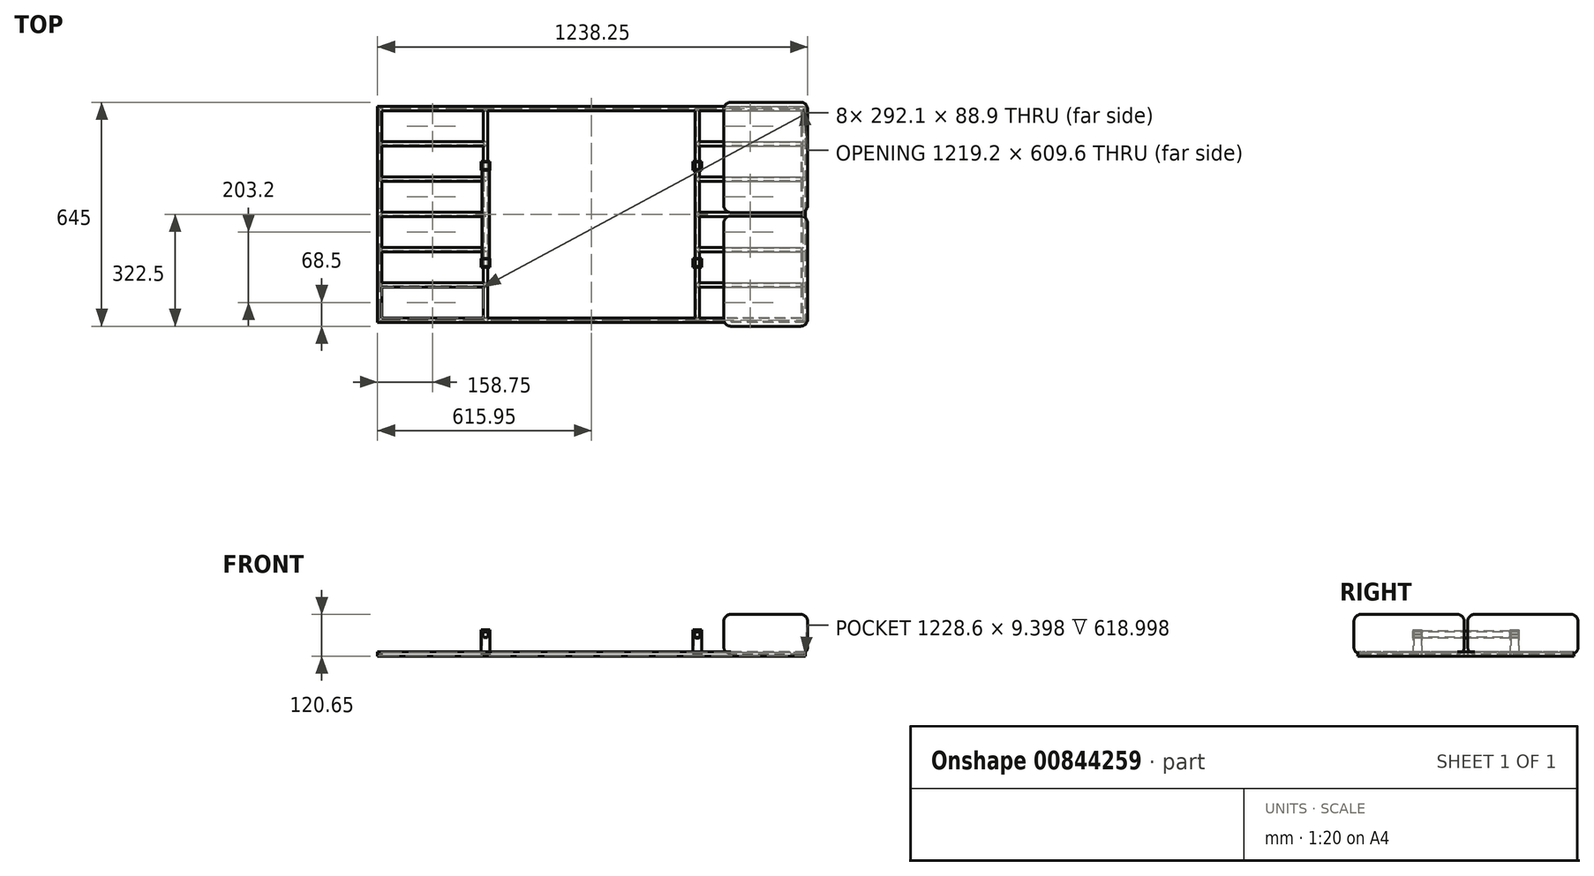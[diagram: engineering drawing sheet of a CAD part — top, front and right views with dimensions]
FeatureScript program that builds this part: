
annotation { "Feature Type Name" : "Feature", "Feature Type Description" : "" }
export const myFeature = defineFeature(function(context is Context, id is Id, definition is map)
    precondition{}
    {
        {
            var Q0;
            Q0=qCreatedBy(makeId("Top.planeOp"),FACE);
            var sketch = newSketch(context, id + "F0", { "sketchPlane" : qUnion([Q0])});
            skLineSegment(sketch, "E0", {"start": v(0, 0) * mm, "end": v(-609.6, 0) * mm});
            skLineSegment(sketch, "E1", {"start": v(-609.6, -609.6) * mm, "end": v(0, -609.6) * mm});
            skLineSegment(sketch, "E2", {"start": v(0, 0) * mm, "end": v(0, -609.6) * mm, "construction": true});
            skLineSegment(sketch, "E3.MirrorCS", {"start": v(609.6, -609.6) * mm, "end": v(0, -609.6) * mm});
            skLineSegment(sketch, "E4.MirrorCS", {"start": v(0, 0) * mm, "end": v(609.6, 0) * mm});
            skLineSegment(sketch, "E5", {"start": v(-304.8, 0) * mm, "end": v(-304.8, -609.6) * mm});
            skLineSegment(sketch, "E6.MirrorCS", {"start": v(304.8, 0) * mm, "end": v(304.8, -609.6) * mm});
            skPoint(sketch, "E7.orphan", {"position": v(508, -304.8) * mm});
            skLineSegment(sketch, "E8", {"start": v(-609.6, 0) * mm, "end": v(-609.6, -609.6) * mm});
            skLineSegment(sketch, "E9", {"start": v(609.6, -609.6) * mm, "end": v(609.6, 0) * mm});
            skLineSegment(sketch, "E10", {"start": v(-609.6, -101.6) * mm, "end": v(-304.8, -101.6) * mm});
            skLineSegment(sketch, "E11", {"start": v(-304.8, -203.2) * mm, "end": v(-609.6, -203.2) * mm});
            skLineSegment(sketch, "E12", {"start": v(-304.8, -304.8) * mm, "end": v(-609.6, -304.8) * mm});
            skLineSegment(sketch, "E13", {"start": v(-304.8, -406.4) * mm, "end": v(-609.6, -406.4) * mm});
            skLineSegment(sketch, "E14", {"start": v(-304.8, -508) * mm, "end": v(-609.6, -508) * mm});
            skLineSegment(sketch, "E15.MirrorCS", {"start": v(304.8, -406.4) * mm, "end": v(609.6, -406.4) * mm});
            skLineSegment(sketch, "E16.MirrorCS", {"start": v(304.8, -203.2) * mm, "end": v(609.6, -203.2) * mm});
            skLineSegment(sketch, "E17.MirrorCS", {"start": v(304.8, -508) * mm, "end": v(609.6, -508) * mm});
            skLineSegment(sketch, "E18.MirrorCS", {"start": v(609.6, -101.6) * mm, "end": v(304.8, -101.6) * mm});
            skLineSegment(sketch, "E19.MirrorCS", {"start": v(304.8, -304.8) * mm, "end": v(609.6, -304.8) * mm});
            skSolve(sketch);
        }
        {
            var Q0;
            Q0=qCreatedBy(makeId("Right.planeOp"),FACE);
            var sketch = newSketch(context, id + "F1", { "sketchPlane" : qUnion([Q0])});
            skLineSegment(sketch, "E20.bottom", {"start": v(-6.35, 6.35) * mm, "end": v(6.35, 6.35) * mm});
            skLineSegment(sketch, "E20.top", {"start": v(-6.35, -6.35) * mm, "end": v(6.35, -6.35) * mm});
            skLineSegment(sketch, "E20.left", {"start": v(-6.35, 6.35) * mm, "end": v(-6.35, -6.35) * mm});
            skLineSegment(sketch, "E20.right", {"start": v(6.35, 6.35) * mm, "end": v(6.35, -6.35) * mm});
            skPoint(sketch, "E20.middle", {"position": v(0, 0) * mm});
            skLineSegment(sketch, "E21.bottom", {"start": v(-4.7, -4.7) * mm, "end": v(4.7, -4.7) * mm});
            skLineSegment(sketch, "E21.top", {"start": v(-4.7, 4.7) * mm, "end": v(4.7, 4.7) * mm});
            skLineSegment(sketch, "E21.left", {"start": v(-4.7, -4.7) * mm, "end": v(-4.7, 4.7) * mm});
            skLineSegment(sketch, "E21.right", {"start": v(4.7, -4.7) * mm, "end": v(4.7, 4.7) * mm});
            skSolve(sketch);
        }
        {
            var Q0;
            Q0=makeQuery(id+"F1.imprint","IMPRINT",FACE,{"disambiguationData":[TD([[makeQuery(id+"F1.imprint","IMPRINT",EDGE,{"derivedFrom":sQuery(id+"F1.wireOp",EDGE,"E20.bottom")}),-1.0]])]});
            var Q1;
            Q1=sQuery(id+"F0.wireOp",EDGE,"E0");
            var Q2;
            Q2=sQuery(id+"F0.wireOp",EDGE,"E8");
            var Q3;
            Q3=sQuery(id+"F0.wireOp",EDGE,"E1");
            var Q4;
            Q4=sQuery(id+"F0.wireOp",EDGE,"E3.MirrorCS");
            var Q5;
            Q5=sQuery(id+"F0.wireOp",EDGE,"E9");
            var Q6;
            Q6=sQuery(id+"F0.wireOp",EDGE,"E4.MirrorCS");
            sweep(context, id + "F2", {"profiles" : qUnion([Q0]), "path" : qUnion([Q1, Q2, Q3, Q4, Q5, Q6])});
        }
        {
            var Q0;
            Q0=qCreatedBy(makeId("Right.planeOp"),FACE);
            cPlane(context, id + "F3", {"entities" : qUnion([Q0]), "cplaneType" : CPlaneType.OFFSET, "offset" : 304.8 * mm, "width" : 150 * mm, "height" : 150 * mm});
        }
        {
            var Q0;
            Q0=qCreatedBy(id+"F3.planeOp",FACE);
            var sketch = newSketch(context, id + "F4", { "sketchPlane" : qUnion([Q0])});
            skCircle(sketch, "E22", {"center": v(-101.6, 0) * mm, "radius": 13.34 * mm, "construction": true});
            skCircle(sketch, "E23", {"center": v(-203.2, 0) * mm, "radius": 13.34 * mm, "construction": true});
            skCircle(sketch, "E24", {"center": v(-304.8, 0) * mm, "radius": 13.34 * mm, "construction": true});
            skCircle(sketch, "E25", {"center": v(-406.4, 0) * mm, "radius": 13.34 * mm, "construction": true});
            skCircle(sketch, "E26", {"center": v(-508, 0) * mm, "radius": 13.34 * mm, "construction": true});
            skCircle(sketch, "E27", {"center": v(-101.6, 0) * mm, "radius": 10.46 * mm, "construction": true});
            skCircle(sketch, "E28", {"center": v(-203.2, 0) * mm, "radius": 10.46 * mm, "construction": true});
            skCircle(sketch, "E29", {"center": v(-304.8, 0) * mm, "radius": 10.46 * mm, "construction": true});
            skCircle(sketch, "E30", {"center": v(-406.4, 0) * mm, "radius": 10.46 * mm, "construction": true});
            skCircle(sketch, "E31", {"center": v(-508, 0) * mm, "radius": 10.46 * mm, "construction": true});
            skLineSegment(sketch, "E32.bottom", {"start": v(-95.25, 6.35) * mm, "end": v(-107.95, 6.35) * mm});
            skLineSegment(sketch, "E32.top", {"start": v(-95.25, -6.35) * mm, "end": v(-107.95, -6.35) * mm});
            skLineSegment(sketch, "E32.left", {"start": v(-95.25, 6.35) * mm, "end": v(-95.25, -6.35) * mm});
            skLineSegment(sketch, "E32.right", {"start": v(-107.95, 6.35) * mm, "end": v(-107.95, -6.35) * mm});
            skLineSegment(sketch, "E33.bottom", {"start": v(-96.9, 4.7) * mm, "end": v(-106.3, 4.7) * mm});
            skLineSegment(sketch, "E33.top", {"start": v(-96.9, -4.7) * mm, "end": v(-106.3, -4.7) * mm});
            skLineSegment(sketch, "E33.left", {"start": v(-96.9, 4.7) * mm, "end": v(-96.9, -4.7) * mm});
            skLineSegment(sketch, "E33.right", {"start": v(-106.3, 4.7) * mm, "end": v(-106.3, -4.7) * mm});
            skLineSegment(sketch, "E34.bottom", {"start": v(-196.85, 6.35) * mm, "end": v(-209.55, 6.35) * mm});
            skLineSegment(sketch, "E34.top", {"start": v(-196.85, -6.35) * mm, "end": v(-209.55, -6.35) * mm});
            skLineSegment(sketch, "E34.left", {"start": v(-196.85, 6.35) * mm, "end": v(-196.85, -6.35) * mm});
            skLineSegment(sketch, "E34.right", {"start": v(-209.55, 6.35) * mm, "end": v(-209.55, -6.35) * mm});
            skLineSegment(sketch, "E35.bottom", {"start": v(-298.45, 6.35) * mm, "end": v(-311.15, 6.35) * mm});
            skLineSegment(sketch, "E35.top", {"start": v(-298.45, -6.35) * mm, "end": v(-311.15, -6.35) * mm});
            skLineSegment(sketch, "E35.left", {"start": v(-298.45, 6.35) * mm, "end": v(-298.45, -6.35) * mm});
            skLineSegment(sketch, "E35.right", {"start": v(-311.15, 6.35) * mm, "end": v(-311.15, -6.35) * mm});
            skLineSegment(sketch, "E36.bottom", {"start": v(-400.05, 6.35) * mm, "end": v(-412.75, 6.35) * mm});
            skLineSegment(sketch, "E36.top", {"start": v(-400.05, -6.35) * mm, "end": v(-412.75, -6.35) * mm});
            skLineSegment(sketch, "E36.left", {"start": v(-400.05, 6.35) * mm, "end": v(-400.05, -6.35) * mm});
            skLineSegment(sketch, "E36.right", {"start": v(-412.75, 6.35) * mm, "end": v(-412.75, -6.35) * mm});
            skLineSegment(sketch, "E37.bottom", {"start": v(-501.65, 6.35) * mm, "end": v(-514.35, 6.35) * mm});
            skLineSegment(sketch, "E37.top", {"start": v(-501.65, -6.35) * mm, "end": v(-514.35, -6.35) * mm});
            skLineSegment(sketch, "E37.left", {"start": v(-501.65, 6.35) * mm, "end": v(-501.65, -6.35) * mm});
            skLineSegment(sketch, "E37.right", {"start": v(-514.35, 6.35) * mm, "end": v(-514.35, -6.35) * mm});
            skLineSegment(sketch, "E38.bottom", {"start": v(-503.3, 4.7) * mm, "end": v(-512.7, 4.7) * mm});
            skLineSegment(sketch, "E38.top", {"start": v(-503.3, -4.7) * mm, "end": v(-512.7, -4.7) * mm});
            skLineSegment(sketch, "E38.left", {"start": v(-503.3, 4.7) * mm, "end": v(-503.3, -4.7) * mm});
            skLineSegment(sketch, "E38.right", {"start": v(-512.7, 4.7) * mm, "end": v(-512.7, -4.7) * mm});
            skLineSegment(sketch, "E39.bottom", {"start": v(-401.7, 4.7) * mm, "end": v(-411.1, 4.7) * mm});
            skLineSegment(sketch, "E39.top", {"start": v(-401.7, -4.7) * mm, "end": v(-411.1, -4.7) * mm});
            skLineSegment(sketch, "E39.left", {"start": v(-401.7, 4.7) * mm, "end": v(-401.7, -4.7) * mm});
            skLineSegment(sketch, "E39.right", {"start": v(-411.1, 4.7) * mm, "end": v(-411.1, -4.7) * mm});
            skLineSegment(sketch, "E40.bottom", {"start": v(-300.1, 4.7) * mm, "end": v(-309.5, 4.7) * mm});
            skLineSegment(sketch, "E40.top", {"start": v(-300.1, -4.7) * mm, "end": v(-309.5, -4.7) * mm});
            skLineSegment(sketch, "E40.left", {"start": v(-300.1, 4.7) * mm, "end": v(-300.1, -4.7) * mm});
            skLineSegment(sketch, "E40.right", {"start": v(-309.5, 4.7) * mm, "end": v(-309.5, -4.7) * mm});
            skLineSegment(sketch, "E41.bottom", {"start": v(-198.5, 4.7) * mm, "end": v(-207.9, 4.7) * mm});
            skLineSegment(sketch, "E41.top", {"start": v(-198.5, -4.7) * mm, "end": v(-207.9, -4.7) * mm});
            skLineSegment(sketch, "E41.left", {"start": v(-198.5, 4.7) * mm, "end": v(-198.5, -4.7) * mm});
            skLineSegment(sketch, "E41.right", {"start": v(-207.9, 4.7) * mm, "end": v(-207.9, -4.7) * mm});
            skSolve(sketch);
        }
        {
            var Q0;
            Q0 = qSketchRegion(id + "F4", true);
            var Q1;
            Q1=sQuery(id+"F0.wireOp",EDGE,"E17.MirrorCS");
            sweep(context, id + "F5", {"operationType" : NewBodyOperationType.ADD, "profiles" : qUnion([Q0]), "path" : qUnion([Q1])});
        }
        {
            var Q0;
            Q0=qCreatedBy(makeId("Right.planeOp"),FACE);
            cPlane(context, id + "F6", {"entities" : qUnion([Q0]), "cplaneType" : CPlaneType.OFFSET, "offset" : 304.8 * mm, "oppositeDirection" : true, "width" : 150 * mm, "height" : 150 * mm});
        }
        {
            var Q0;
            Q0=qCreatedBy(id+"F6.planeOp",FACE);
            var sketch = newSketch(context, id + "F7", { "sketchPlane" : qUnion([Q0])});
            skCircle(sketch, "E42", {"center": v(-101.6, 0) * mm, "radius": 13.33 * mm, "construction": true});
            skCircle(sketch, "E43", {"center": v(-203.2, 0) * mm, "radius": 13.34 * mm, "construction": true});
            skCircle(sketch, "E44", {"center": v(-304.8, 0) * mm, "radius": 13.34 * mm, "construction": true});
            skCircle(sketch, "E45", {"center": v(-406.4, 0) * mm, "radius": 13.34 * mm, "construction": true});
            skCircle(sketch, "E46", {"center": v(-508, 0) * mm, "radius": 13.34 * mm, "construction": true});
            skCircle(sketch, "E47.0", {"center": v(-101.6, 0) * mm, "radius": 10.46 * mm, "construction": true});
            skCircle(sketch, "E48.0", {"center": v(-203.2, 0) * mm, "radius": 10.46 * mm, "construction": true});
            skCircle(sketch, "E49.0", {"center": v(-304.8, 0) * mm, "radius": 10.46 * mm, "construction": true});
            skCircle(sketch, "E50.0", {"center": v(-406.4, 0) * mm, "radius": 10.46 * mm, "construction": true});
            skCircle(sketch, "E51.0", {"center": v(-508, 0) * mm, "radius": 10.46 * mm, "construction": true});
            skLineSegment(sketch, "E52.bottom", {"start": v(-95.25, 6.35) * mm, "end": v(-107.95, 6.35) * mm});
            skLineSegment(sketch, "E52.top", {"start": v(-95.25, -6.35) * mm, "end": v(-107.95, -6.35) * mm});
            skLineSegment(sketch, "E52.left", {"start": v(-95.25, 6.35) * mm, "end": v(-95.25, -6.35) * mm});
            skLineSegment(sketch, "E52.right", {"start": v(-107.95, 6.35) * mm, "end": v(-107.95, -6.35) * mm});
            skLineSegment(sketch, "E53.bottom", {"start": v(-96.9, 4.7) * mm, "end": v(-106.3, 4.7) * mm});
            skLineSegment(sketch, "E53.top", {"start": v(-96.9, -4.7) * mm, "end": v(-106.3, -4.7) * mm});
            skLineSegment(sketch, "E53.left", {"start": v(-96.9, 4.7) * mm, "end": v(-96.9, -4.7) * mm});
            skLineSegment(sketch, "E53.right", {"start": v(-106.3, 4.7) * mm, "end": v(-106.3, -4.7) * mm});
            skLineSegment(sketch, "E54.1.0.0", {"start": v(-196.85, 6.35) * mm, "end": v(-209.55, 6.35) * mm});
            skLineSegment(sketch, "E54.1.0.1", {"start": v(-209.55, 6.35) * mm, "end": v(-209.55, -6.35) * mm});
            skLineSegment(sketch, "E54.1.0.2", {"start": v(-196.85, -6.35) * mm, "end": v(-209.55, -6.35) * mm});
            skLineSegment(sketch, "E54.1.0.3", {"start": v(-196.85, 6.35) * mm, "end": v(-196.85, -6.35) * mm});
            skLineSegment(sketch, "E54.1.0.4", {"start": v(-198.5, 4.7) * mm, "end": v(-198.5, -4.7) * mm});
            skLineSegment(sketch, "E54.1.0.5", {"start": v(-198.5, 4.7) * mm, "end": v(-207.9, 4.7) * mm});
            skLineSegment(sketch, "E54.1.0.6", {"start": v(-207.9, 4.7) * mm, "end": v(-207.9, -4.7) * mm});
            skLineSegment(sketch, "E54.1.0.7", {"start": v(-198.5, -4.7) * mm, "end": v(-207.9, -4.7) * mm});
            skLineSegment(sketch, "E54.2.0.0", {"start": v(-298.45, 6.35) * mm, "end": v(-311.15, 6.35) * mm});
            skLineSegment(sketch, "E54.2.0.1", {"start": v(-311.15, 6.35) * mm, "end": v(-311.15, -6.35) * mm});
            skLineSegment(sketch, "E54.2.0.2", {"start": v(-298.45, -6.35) * mm, "end": v(-311.15, -6.35) * mm});
            skLineSegment(sketch, "E54.2.0.3", {"start": v(-298.45, 6.35) * mm, "end": v(-298.45, -6.35) * mm});
            skLineSegment(sketch, "E54.2.0.4", {"start": v(-300.1, 4.7) * mm, "end": v(-300.1, -4.7) * mm});
            skLineSegment(sketch, "E54.2.0.5", {"start": v(-300.1, 4.7) * mm, "end": v(-309.5, 4.7) * mm});
            skLineSegment(sketch, "E54.2.0.6", {"start": v(-309.5, 4.7) * mm, "end": v(-309.5, -4.7) * mm});
            skLineSegment(sketch, "E54.2.0.7", {"start": v(-300.1, -4.7) * mm, "end": v(-309.5, -4.7) * mm});
            skLineSegment(sketch, "E54.3.0.0", {"start": v(-400.05, 6.35) * mm, "end": v(-412.75, 6.35) * mm});
            skLineSegment(sketch, "E54.3.0.1", {"start": v(-412.75, 6.35) * mm, "end": v(-412.75, -6.35) * mm});
            skLineSegment(sketch, "E54.3.0.2", {"start": v(-400.05, -6.35) * mm, "end": v(-412.75, -6.35) * mm});
            skLineSegment(sketch, "E54.3.0.3", {"start": v(-400.05, 6.35) * mm, "end": v(-400.05, -6.35) * mm});
            skLineSegment(sketch, "E54.3.0.4", {"start": v(-401.7, 4.7) * mm, "end": v(-401.7, -4.7) * mm});
            skLineSegment(sketch, "E54.3.0.5", {"start": v(-401.7, 4.7) * mm, "end": v(-411.1, 4.7) * mm});
            skLineSegment(sketch, "E54.3.0.6", {"start": v(-411.1, 4.7) * mm, "end": v(-411.1, -4.7) * mm});
            skLineSegment(sketch, "E54.3.0.7", {"start": v(-401.7, -4.7) * mm, "end": v(-411.1, -4.7) * mm});
            skLineSegment(sketch, "E54.4.0.0", {"start": v(-501.65, 6.35) * mm, "end": v(-514.35, 6.35) * mm});
            skLineSegment(sketch, "E54.4.0.1", {"start": v(-514.35, 6.35) * mm, "end": v(-514.35, -6.35) * mm});
            skLineSegment(sketch, "E54.4.0.2", {"start": v(-501.65, -6.35) * mm, "end": v(-514.35, -6.35) * mm});
            skLineSegment(sketch, "E54.4.0.3", {"start": v(-501.65, 6.35) * mm, "end": v(-501.65, -6.35) * mm});
            skLineSegment(sketch, "E54.4.0.4", {"start": v(-503.3, 4.7) * mm, "end": v(-503.3, -4.7) * mm});
            skLineSegment(sketch, "E54.4.0.5", {"start": v(-503.3, 4.7) * mm, "end": v(-512.7, 4.7) * mm});
            skLineSegment(sketch, "E54.4.0.6", {"start": v(-512.7, 4.7) * mm, "end": v(-512.7, -4.7) * mm});
            skLineSegment(sketch, "E54.4.0.7", {"start": v(-503.3, -4.7) * mm, "end": v(-512.7, -4.7) * mm});
            skLineSegment(sketch, "E54.direction1", {"start": v(-107.95, 6.35) * mm, "end": v(-209.55, 6.35) * mm, "construction": true});
            skSolve(sketch);
        }
        {
            var Q0;
            Q0 = qSketchRegion(id + "F7", true);
            var Q1;
            Q1=sQuery(id+"F0.wireOp",EDGE,"E14");
            sweep(context, id + "F8", {"operationType" : NewBodyOperationType.ADD, "profiles" : qUnion([Q0]), "path" : qUnion([Q1])});
        }
        {
            var Q0;
            Q0=qCreatedBy(makeId("Front.planeOp"),FACE);
            cPlane(context, id + "F9", {"entities" : qUnion([Q0]), "cplaneType" : CPlaneType.OFFSET, "offset" : (609.6 / 2) * mm, "width" : 150 * mm, "height" : 150 * mm});
        }
        {
            var Q0;
            Q0=qCreatedBy(id+"F9.planeOp",FACE);
            var sketch = newSketch(context, id + "F10", { "sketchPlane" : qUnion([Q0])});
            skCircle(sketch, "E55", {"center": v(-304.8, 0) * mm, "radius": 13.34 * mm, "construction": true});
            skLineSegment(sketch, "E56", {"start": v(0, 161.47) * mm, "end": v(0, -177.5) * mm, "construction": true});
            skCircle(sketch, "E57.MirrorC", {"center": v(304.8, 0) * mm, "radius": 13.34 * mm, "construction": true});
            skCircle(sketch, "E58", {"center": v(-304.8, 0) * mm, "radius": 10.46 * mm, "construction": true});
            skCircle(sketch, "E59", {"center": v(304.8, 0) * mm, "radius": 10.46 * mm, "construction": true});
            skLineSegment(sketch, "E60.bottom", {"start": v(-298.45, 6.35) * mm, "end": v(-311.15, 6.35) * mm});
            skLineSegment(sketch, "E60.top", {"start": v(-298.45, -6.35) * mm, "end": v(-311.15, -6.35) * mm});
            skLineSegment(sketch, "E60.left", {"start": v(-298.45, 6.35) * mm, "end": v(-298.45, -6.35) * mm});
            skLineSegment(sketch, "E60.right", {"start": v(-311.15, 6.35) * mm, "end": v(-311.15, -6.35) * mm});
            skLineSegment(sketch, "E61.bottom", {"start": v(-300.1, 4.7) * mm, "end": v(-309.5, 4.7) * mm});
            skLineSegment(sketch, "E61.top", {"start": v(-300.1, -4.7) * mm, "end": v(-309.5, -4.7) * mm});
            skLineSegment(sketch, "E61.left", {"start": v(-300.1, 4.7) * mm, "end": v(-300.1, -4.7) * mm});
            skLineSegment(sketch, "E61.right", {"start": v(-309.5, 4.7) * mm, "end": v(-309.5, -4.7) * mm});
            skLineSegment(sketch, "E62.MirrorCS", {"start": v(298.45, 6.35) * mm, "end": v(311.15, 6.35) * mm});
            skLineSegment(sketch, "E63.MirrorCS", {"start": v(300.1, 4.7) * mm, "end": v(309.5, 4.7) * mm});
            skLineSegment(sketch, "E64.MirrorCS", {"start": v(298.45, 6.35) * mm, "end": v(298.45, -6.35) * mm});
            skLineSegment(sketch, "E65.MirrorCS", {"start": v(300.1, 4.7) * mm, "end": v(300.1, -4.7) * mm});
            skLineSegment(sketch, "E66.MirrorCS", {"start": v(300.1, -4.7) * mm, "end": v(309.5, -4.7) * mm});
            skLineSegment(sketch, "E67.MirrorCS", {"start": v(298.45, -6.35) * mm, "end": v(311.15, -6.35) * mm});
            skLineSegment(sketch, "E68.MirrorCS", {"start": v(309.5, 4.7) * mm, "end": v(309.5, -4.7) * mm});
            skLineSegment(sketch, "E69.MirrorCS", {"start": v(311.15, 6.35) * mm, "end": v(311.15, -6.35) * mm});
            skSolve(sketch);
        }
        {
            var Q0;
            Q0=makeQuery(id+"F10.imprint","IMPRINT",FACE,{"disambiguationData":[TD([[makeQuery(id+"F10.imprint","IMPRINT",EDGE,{"derivedFrom":sQuery(id+"F10.wireOp",EDGE,"E60.bottom")}),1.0]])]});
            var Q1;
            Q1=makeQuery(id+"F10.imprint","IMPRINT",FACE,{"disambiguationData":[TD([[makeQuery(id+"F10.imprint","IMPRINT",EDGE,{"derivedFrom":sQuery(id+"F10.wireOp",EDGE,"E62.MirrorCS")}),-1.0]])]});
            var Q2;
            Q2=sQuery(id+"F0.wireOp",EDGE,"E5");
            sweep(context, id + "F11", {"operationType" : NewBodyOperationType.ADD, "profiles" : qUnion([Q0, Q1]), "path" : qUnion([Q2])});
        }
        {
            var Q0;
            Q0=qCreatedBy(makeId("Top.planeOp"),FACE);
            var sketch = newSketch(context, id + "F12", { "sketchPlane" : qUnion([Q0])});
            skLineSegment(sketch, "E70.bottom", {"start": v(622.3, 17.7) * mm, "end": v(381, 17.7) * mm});
            skLineSegment(sketch, "E70.top", {"start": v(622.3, -299.8) * mm, "end": v(381, -299.8) * mm});
            skLineSegment(sketch, "E70.left", {"start": v(622.3, 17.7) * mm, "end": v(622.3, -299.8) * mm});
            skLineSegment(sketch, "E70.right", {"start": v(381, 17.7) * mm, "end": v(381, -299.8) * mm});
            skPoint(sketch, "E70.middle", {"position": v(501.65, -141.05) * mm});
            skPoint(sketch, "E71.0", {"position": v(508, -304.8) * mm});
            skLineSegment(sketch, "E72.0", {"start": v(304.8, 0) * mm, "end": v(304.8, -609.6) * mm, "construction": true});
            skLineSegment(sketch, "E73", {"start": v(508, -304.8) * mm, "end": v(752.08, -304.8) * mm, "construction": true});
            skLineSegment(sketch, "E74.MirrorCS", {"start": v(622.3, -309.8) * mm, "end": v(381, -309.8) * mm});
            skLineSegment(sketch, "E75.MirrorCS", {"start": v(622.3, -627.3) * mm, "end": v(622.3, -309.8) * mm});
            skLineSegment(sketch, "E76.MirrorCS", {"start": v(622.3, -627.3) * mm, "end": v(381, -627.3) * mm});
            skLineSegment(sketch, "E77.MirrorCS", {"start": v(381, -627.3) * mm, "end": v(381, -309.8) * mm});
            skSolve(sketch);
        }
        {
            var Q0;
            Q0 = qSketchRegion(id + "F12", true);
            extrude(context, id + "F13", {"entities" : qUnion([Q0]), "depth" : 114.3 * mm, "offsetDistance" : 25 * mm});
        }
        {
            var Q0;
            Q0=makeQuery(id+"F13.opExtrude","CAP_FACE",FACE,{"disambiguationData":[OSD([sQuery(id+"F12.wireOp",EDGE,"E70.bottom"),sQuery(id+"F12.wireOp",EDGE,"E70.top"),sQuery(id+"F12.wireOp",EDGE,"E70.left"),sQuery(id+"F12.wireOp",EDGE,"E70.right")])],"isStart":false});
            var Q1;
            Q1=makeQuery(id+"F13.opExtrude","CAP_FACE",FACE,{"disambiguationData":[OSD([sQuery(id+"F12.wireOp",EDGE,"E74.MirrorCS"),sQuery(id+"F12.wireOp",EDGE,"E75.MirrorCS"),sQuery(id+"F12.wireOp",EDGE,"E76.MirrorCS"),sQuery(id+"F12.wireOp",EDGE,"E77.MirrorCS")])],"isStart":false});
            var Q2;
            Q2=makeQuery(id+"F13.opExtrude","SWEPT_FACE",FACE,{"disambiguationData":[OSD([sQuery(id+"F12.wireOp",EDGE,"E75.MirrorCS")])]});
            var Q3;
            Q3=makeQuery(id+"F13.opExtrude","SWEPT_FACE",FACE,{"disambiguationData":[OSD([sQuery(id+"F12.wireOp",EDGE,"E70.left")])]});
            var Q4;
            Q4=makeQuery(id+"F13.opExtrude","CAP_FACE",FACE,{"disambiguationData":[OSD([sQuery(id+"F12.wireOp",EDGE,"E70.bottom"),sQuery(id+"F12.wireOp",EDGE,"E70.top"),sQuery(id+"F12.wireOp",EDGE,"E70.left"),sQuery(id+"F12.wireOp",EDGE,"E70.right")])],"isStart":true});
            var Q5;
            Q5=makeQuery(id+"F13.opExtrude","CAP_FACE",FACE,{"disambiguationData":[OSD([sQuery(id+"F12.wireOp",EDGE,"E74.MirrorCS"),sQuery(id+"F12.wireOp",EDGE,"E75.MirrorCS"),sQuery(id+"F12.wireOp",EDGE,"E76.MirrorCS"),sQuery(id+"F12.wireOp",EDGE,"E77.MirrorCS")])],"isStart":true});
            var Q6;
            Q6=makeQuery(id+"F13.opExtrude","SWEPT_FACE",FACE,{"disambiguationData":[OSD([sQuery(id+"F12.wireOp",EDGE,"E77.MirrorCS")])]});
            var Q7;
            Q7=makeQuery(id+"F13.opExtrude","SWEPT_FACE",FACE,{"disambiguationData":[OSD([sQuery(id+"F12.wireOp",EDGE,"E70.right")])]});
            fillet(context, id + "F14", {"entities" : qUnion([Q0, Q1, Q2, Q3, Q4, Q5, Q6, Q7]), "radius" : 20 * mm, "tangentPropagation" : true, "allowEdgeOverflow" : false});
        }
        {
            var Q0;
            {var subQ0=sQuery(id+"F0.wireOp",EDGE,"E5");var subQ1=sQuery(id+"F0.wireOp",EDGE,"E14");var subQ2=sQuery(id+"F0.wireOp",EDGE,"E17.MirrorCS");Q0=makeQuery(id+"F11.boolean.opBoolean","MERGE",FACE,{"derivedFrom":[makeQuery(id+"F8.boolean.opBoolean","MERGE",FACE,{"derivedFrom":[makeQuery(id+"F5.boolean.opBoolean","MERGE",FACE,{"derivedFrom":[makeQuery(id+"F2.opSweep","SWEPT_FACE",FACE,{"disambiguationData":[OSD([sQuery(id+"F0.wireOp",EDGE,"E8"),sQuery(id+"F1.wireOp",EDGE,"E20.top")])]}),makeQuery(id+"F5.opSweep","SWEPT_FACE",FACE,{"disambiguationData":[OSD([subQ2,sQuery(id+"F4.wireOp",EDGE,"E32.top")])]}),makeQuery(id+"F5.opSweep","SWEPT_FACE",FACE,{"disambiguationData":[OSD([subQ2,sQuery(id+"F4.wireOp",EDGE,"E34.top")])]}),makeQuery(id+"F5.opSweep","SWEPT_FACE",FACE,{"disambiguationData":[OSD([subQ2,sQuery(id+"F4.wireOp",EDGE,"E35.top")])]}),makeQuery(id+"F5.opSweep","SWEPT_FACE",FACE,{"disambiguationData":[OSD([subQ2,sQuery(id+"F4.wireOp",EDGE,"E36.top")])]}),makeQuery(id+"F5.opSweep","SWEPT_FACE",FACE,{"disambiguationData":[OSD([subQ2,sQuery(id+"F4.wireOp",EDGE,"E37.top")])]})]}),makeQuery(id+"F8.opSweep","SWEPT_FACE",FACE,{"disambiguationData":[OSD([subQ1,sQuery(id+"F7.wireOp",EDGE,"E52.top")])]}),makeQuery(id+"F8.opSweep","SWEPT_FACE",FACE,{"disambiguationData":[OSD([subQ1,sQuery(id+"F7.wireOp",EDGE,"E54.1.0.2")])]}),makeQuery(id+"F8.opSweep","SWEPT_FACE",FACE,{"disambiguationData":[OSD([subQ1,sQuery(id+"F7.wireOp",EDGE,"E54.2.0.2")])]}),makeQuery(id+"F8.opSweep","SWEPT_FACE",FACE,{"disambiguationData":[OSD([subQ1,sQuery(id+"F7.wireOp",EDGE,"E54.3.0.2")])]}),makeQuery(id+"F8.opSweep","SWEPT_FACE",FACE,{"disambiguationData":[OSD([subQ1,sQuery(id+"F7.wireOp",EDGE,"E54.4.0.2")])]})]}),makeQuery(id+"F11.opSweep","SWEPT_FACE",FACE,{"disambiguationData":[OSD([subQ0,sQuery(id+"F10.wireOp",EDGE,"E60.top")])]}),makeQuery(id+"F11.opSweep","SWEPT_FACE",FACE,{"disambiguationData":[OSD([subQ0,sQuery(id+"F10.wireOp",EDGE,"E67.MirrorCS")])]})]});}
            var sketch = newSketch(context, id + "F15", { "sketchPlane" : qUnion([Q0])});
            skLineSegment(sketch, "E78.bottom", {"start": v(-292.1, 457.2) * mm, "end": v(-317.5, 457.2) * mm});
            skLineSegment(sketch, "E78.top", {"start": v(-292.1, 431.8) * mm, "end": v(-317.5, 431.8) * mm});
            skLineSegment(sketch, "E78.left", {"start": v(-292.1, 457.2) * mm, "end": v(-292.1, 431.8) * mm});
            skLineSegment(sketch, "E78.right", {"start": v(-317.5, 457.2) * mm, "end": v(-317.5, 431.8) * mm});
            skPoint(sketch, "E78.middle", {"position": v(-304.8, 444.5) * mm});
            skLineSegment(sketch, "E79.bottom", {"start": v(-292.1, 177.8) * mm, "end": v(-317.5, 177.8) * mm});
            skLineSegment(sketch, "E79.top", {"start": v(-292.1, 152.4) * mm, "end": v(-317.5, 152.4) * mm});
            skLineSegment(sketch, "E79.left", {"start": v(-292.1, 177.8) * mm, "end": v(-292.1, 152.4) * mm});
            skLineSegment(sketch, "E79.right", {"start": v(-317.5, 177.8) * mm, "end": v(-317.5, 152.4) * mm});
            skPoint(sketch, "E79.middle", {"position": v(-304.8, 165.1) * mm});
            skPoint(sketch, "E79.middle.positionSnap0", {"position": v(-304.8, 431.8) * mm});
            skPoint(sketch, "E79.centerSnap0", {"position": v(-304.8, 431.8) * mm});
            skLineSegment(sketch, "E80", {"start": v(0, 0) * mm, "end": v(0, 682.75) * mm, "construction": true});
            skPoint(sketch, "E80.endSnap0", {"position": v(0, 615.95) * mm});
            skLineSegment(sketch, "E81.MirrorCS", {"start": v(317.5, 177.8) * mm, "end": v(317.5, 152.4) * mm});
            skLineSegment(sketch, "E82.MirrorCS", {"start": v(292.1, 457.2) * mm, "end": v(317.5, 457.2) * mm});
            skLineSegment(sketch, "E83.MirrorCS", {"start": v(292.1, 431.8) * mm, "end": v(317.5, 431.8) * mm});
            skLineSegment(sketch, "E84.MirrorCS", {"start": v(292.1, 152.4) * mm, "end": v(317.5, 152.4) * mm});
            skLineSegment(sketch, "E85.MirrorCS", {"start": v(292.1, 177.8) * mm, "end": v(292.1, 152.4) * mm});
            skLineSegment(sketch, "E86.MirrorCS", {"start": v(292.1, 457.2) * mm, "end": v(292.1, 431.8) * mm});
            skLineSegment(sketch, "E87.MirrorCS", {"start": v(292.1, 177.8) * mm, "end": v(317.5, 177.8) * mm});
            skLineSegment(sketch, "E88.MirrorCS", {"start": v(317.5, 457.2) * mm, "end": v(317.5, 431.8) * mm});
            skPoint(sketch, "E89.MirrorP", {"position": v(304.8, 431.8) * mm});
            skPoint(sketch, "E90.MirrorP", {"position": v(304.8, 444.5) * mm});
            skPoint(sketch, "E91.MirrorP", {"position": v(304.8, 165.1) * mm});
            skLineSegment(sketch, "E92.bottom", {"start": v(-294.2, 175.7) * mm, "end": v(-315.4, 175.7) * mm});
            skLineSegment(sketch, "E92.top", {"start": v(-294.2, 154.5) * mm, "end": v(-315.4, 154.5) * mm});
            skLineSegment(sketch, "E92.left", {"start": v(-294.2, 175.7) * mm, "end": v(-294.2, 154.5) * mm});
            skLineSegment(sketch, "E92.right", {"start": v(-315.4, 175.7) * mm, "end": v(-315.4, 154.5) * mm});
            skLineSegment(sketch, "E93.bottom", {"start": v(-294.2, 455.1) * mm, "end": v(-315.4, 455.1) * mm});
            skLineSegment(sketch, "E93.top", {"start": v(-294.2, 433.9) * mm, "end": v(-315.4, 433.9) * mm});
            skLineSegment(sketch, "E93.left", {"start": v(-294.2, 455.1) * mm, "end": v(-294.2, 433.9) * mm});
            skLineSegment(sketch, "E93.right", {"start": v(-315.4, 455.1) * mm, "end": v(-315.4, 433.9) * mm});
            skLineSegment(sketch, "E94.MirrorCS", {"start": v(294.2, 455.1) * mm, "end": v(294.2, 433.9) * mm});
            skLineSegment(sketch, "E95.MirrorCS", {"start": v(294.2, 455.1) * mm, "end": v(315.4, 455.1) * mm});
            skLineSegment(sketch, "E96.MirrorCS", {"start": v(315.4, 455.1) * mm, "end": v(315.4, 433.9) * mm});
            skLineSegment(sketch, "E97.MirrorCS", {"start": v(294.2, 433.9) * mm, "end": v(315.4, 433.9) * mm});
            skLineSegment(sketch, "E98.MirrorCS", {"start": v(315.4, 175.7) * mm, "end": v(315.4, 154.5) * mm});
            skLineSegment(sketch, "E99.MirrorCS", {"start": v(294.2, 175.7) * mm, "end": v(294.2, 154.5) * mm});
            skLineSegment(sketch, "E100.MirrorCS", {"start": v(294.2, 175.7) * mm, "end": v(315.4, 175.7) * mm});
            skLineSegment(sketch, "E101.MirrorCS", {"start": v(294.2, 154.5) * mm, "end": v(315.4, 154.5) * mm});
            skSolve(sketch);
        }
        {
            var Q0;
            Q0 = qSketchRegion(id + "F15", true);
            extrude(context, id + "F16", {"entities" : qUnion([Q0]), "operationType" : NewBodyOperationType.ADD, "oppositeDirection" : true, "depth" : 76.2 * mm, "offsetDistance" : 25 * mm});
        }
        {
            var Q0;
            {var subQ9=sQuery(id+"F15.wireOp",EDGE,"E78.left");var subQ11=sQuery(id+"F15.wireOp",EDGE,"E78.bottom");Q0=makeQuery(id+"F16.boolean.opBoolean","SPLIT",FACE,{"disambiguationData":[TD([makeQuery(id+"F16.opExtrude","SWEPT_FACE",FACE,{"disambiguationData":[OSD([subQ9])]})])],"derivedFrom":makeQuery(id+"F16.opExtrude","SWEPT_FACE",FACE,{"disambiguationData":[OSD([subQ11])]})});}
            var sketch = newSketch(context, id + "F17", { "sketchPlane" : qUnion([Q0])});
            skCircle(sketch, "E102", {"center": v(-304.8, 56) * mm, "radius": 10.67 * mm});
            skLineSegment(sketch, "E103", {"start": v(0, 0) * mm, "end": v(0, 97.3) * mm, "construction": true});
            skCircle(sketch, "E104.MirrorC", {"center": v(304.8, 56) * mm, "radius": 10.67 * mm});
            skCircle(sketch, "E105", {"center": v(-304.8, 56) * mm, "radius": 7.9 * mm});
            skCircle(sketch, "E106.MirrorC", {"center": v(304.8, 56) * mm, "radius": 7.9 * mm});
            skSolve(sketch);
        }
        {
            var Q0;
            Q0=makeQuery(id+"F17.imprint","IMPRINT",FACE,{"disambiguationData":[TD([[makeQuery(id+"F17.imprint","IMPRINT",EDGE,{"derivedFrom":sQuery(id+"F17.wireOp",EDGE,"E105")}),1.0]])]});
            var Q1;
            Q1=makeQuery(id+"F17.imprint","IMPRINT",FACE,{"disambiguationData":[TD([[makeQuery(id+"F17.imprint","IMPRINT",EDGE,{"derivedFrom":sQuery(id+"F17.wireOp",EDGE,"E106.MirrorC")}),-1.0]])]});
            extrude(context, id + "F18", {"entities" : qUnion([Q0, Q1]), "operationType" : NewBodyOperationType.REMOVE, "endBound" : BoundingType.THROUGH_ALL, "oppositeDirection" : true, "depth" : 25 * mm, "offsetDistance" : 25 * mm});
        }
        {
            var Q0;
            Q0=makeQuery(id+"F17.imprint","IMPRINT",FACE,{"disambiguationData":[TD([[makeQuery(id+"F17.imprint","IMPRINT",EDGE,{"derivedFrom":sQuery(id+"F17.wireOp",EDGE,"E104.MirrorC")}),-1.0]])]});
            var Q1;
            Q1=makeQuery(id+"F17.imprint","IMPRINT",FACE,{"disambiguationData":[TD([[makeQuery(id+"F17.imprint","IMPRINT",EDGE,{"derivedFrom":sQuery(id+"F17.wireOp",EDGE,"E102")}),1.0]])]});
            var Q2;
            {var subQ9=sQuery(id+"F15.wireOp",EDGE,"E79.left");var subQ10=sQuery(id+"F15.wireOp",EDGE,"E79.top");Q2=makeQuery(id+"F16.boolean.opBoolean","SPLIT",FACE,{"disambiguationData":[TD([makeQuery(id+"F16.opExtrude","SWEPT_FACE",FACE,{"disambiguationData":[OSD([subQ9])]})])],"derivedFrom":makeQuery(id+"F16.opExtrude","SWEPT_FACE",FACE,{"disambiguationData":[OSD([subQ10])]})});}
            extrude(context, id + "F19", {"entities" : qUnion([Q0, Q1]), "operationType" : NewBodyOperationType.ADD, "endBound" : BoundingType.UP_TO_SURFACE, "oppositeDirection" : true, "depth" : 25 * mm, "endBoundEntityFace" : qUnion([Q2]), "offsetDistance" : 25 * mm});
        }
    });
